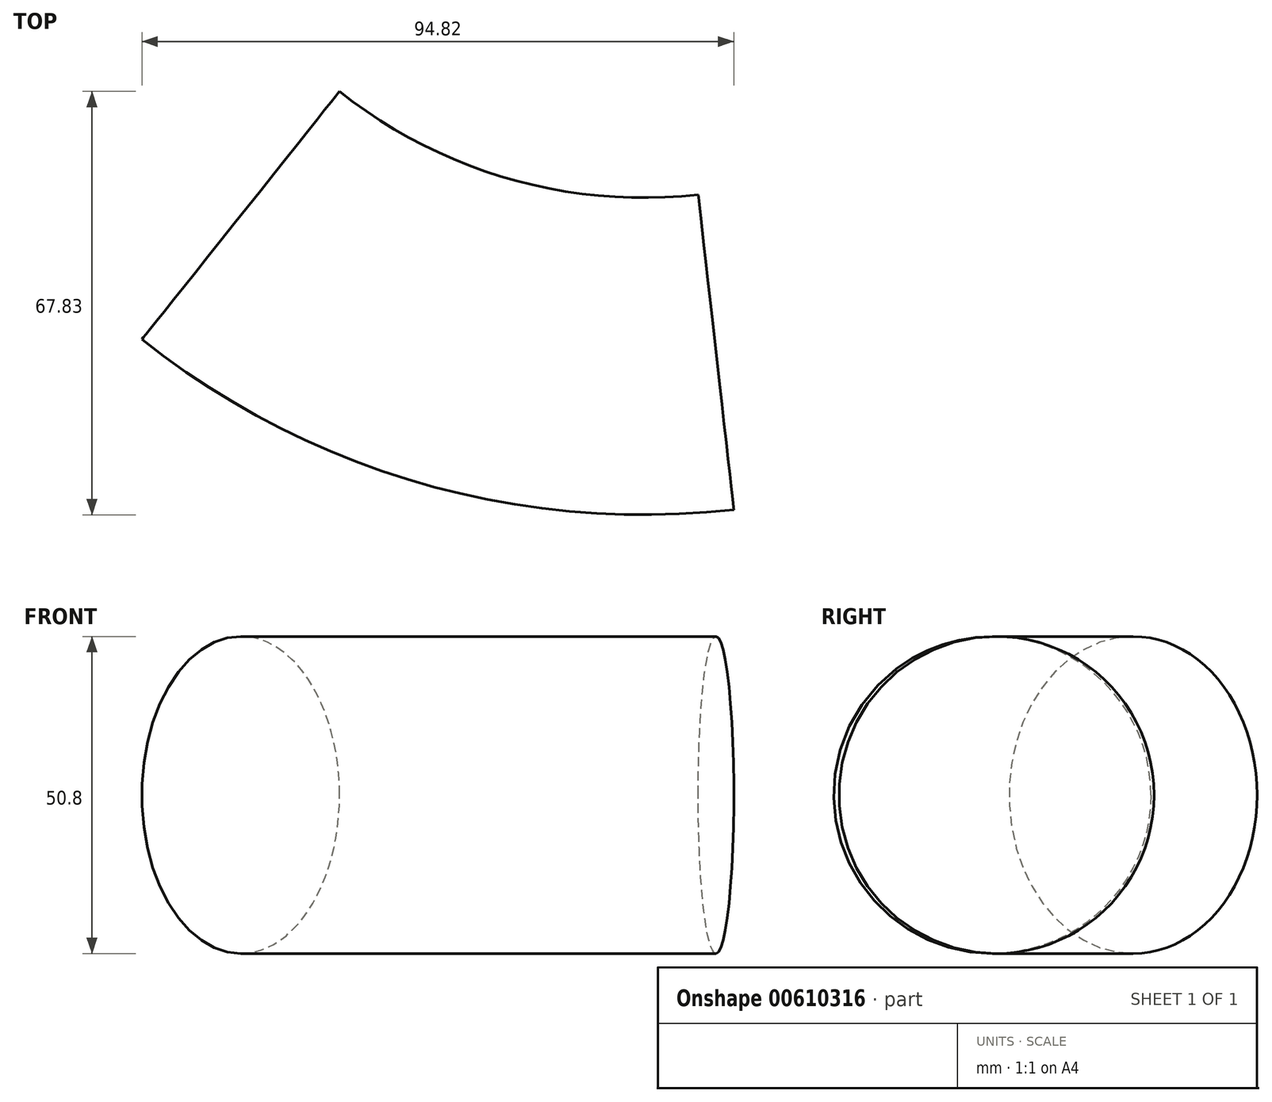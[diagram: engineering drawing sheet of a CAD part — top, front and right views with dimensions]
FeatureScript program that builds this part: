
annotation { "Feature Type Name" : "Feature", "Feature Type Description" : "" }
export const myFeature = defineFeature(function(context is Context, id is Id, definition is map)
    precondition{}
    {
        {
            var Q0;
            Q0=qCreatedBy(makeId("Top.planeOp"),FACE);
            var sketch = newSketch(context, id + "F0", { "sketchPlane" : qUnion([Q0])});
            skArc(sketch, "E0", {"start": v(-38.2, 13.6) * mm, "mid": v(-2.28, -4.94) * mm, "end": v(38, -8.33) * mm});
            skSolve(sketch);
        }
        {
            var Q0;
            Q0=sQuery(id+"F0.wireOp",VERTEX,"E0.end");
            var Q1;
            Q1=sQuery(id+"F0.wireOp",EDGE,"E0");
            cPlane(context, id + "F1", {"entities" : qUnion([Q0, Q1]), "cplaneType" : CPlaneType.CURVE_POINT, "offset" : 25.4 * mm, "width" : 152.4 * mm, "height" : 152.4 * mm});
        }
        {
            var Q0;
            Q0=qCreatedBy(id+"F1.planeOp",FACE);
            var sketch = newSketch(context, id + "F2", { "sketchPlane" : qUnion([Q0])});
            skCircle(sketch, "E1", {"center": v(-12.46, 0) * mm, "radius": 25.4 * mm});
            skSolve(sketch);
        }
        {
            var Q0;
            Q0=makeQuery(id+"F2.imprint","IMPRINT",FACE,{"disambiguationData":[TD([[makeQuery(id+"F2.imprint","IMPRINT",EDGE,{"derivedFrom":sQuery(id+"F2.wireOp",EDGE,"E1")}),1.0]])]});
            var Q1;
            Q1=sQuery(id+"F0.wireOp",EDGE,"E0");
            sweep(context, id + "F3", {"profiles" : qUnion([Q0]), "path" : qUnion([Q1])});
        }
    });
